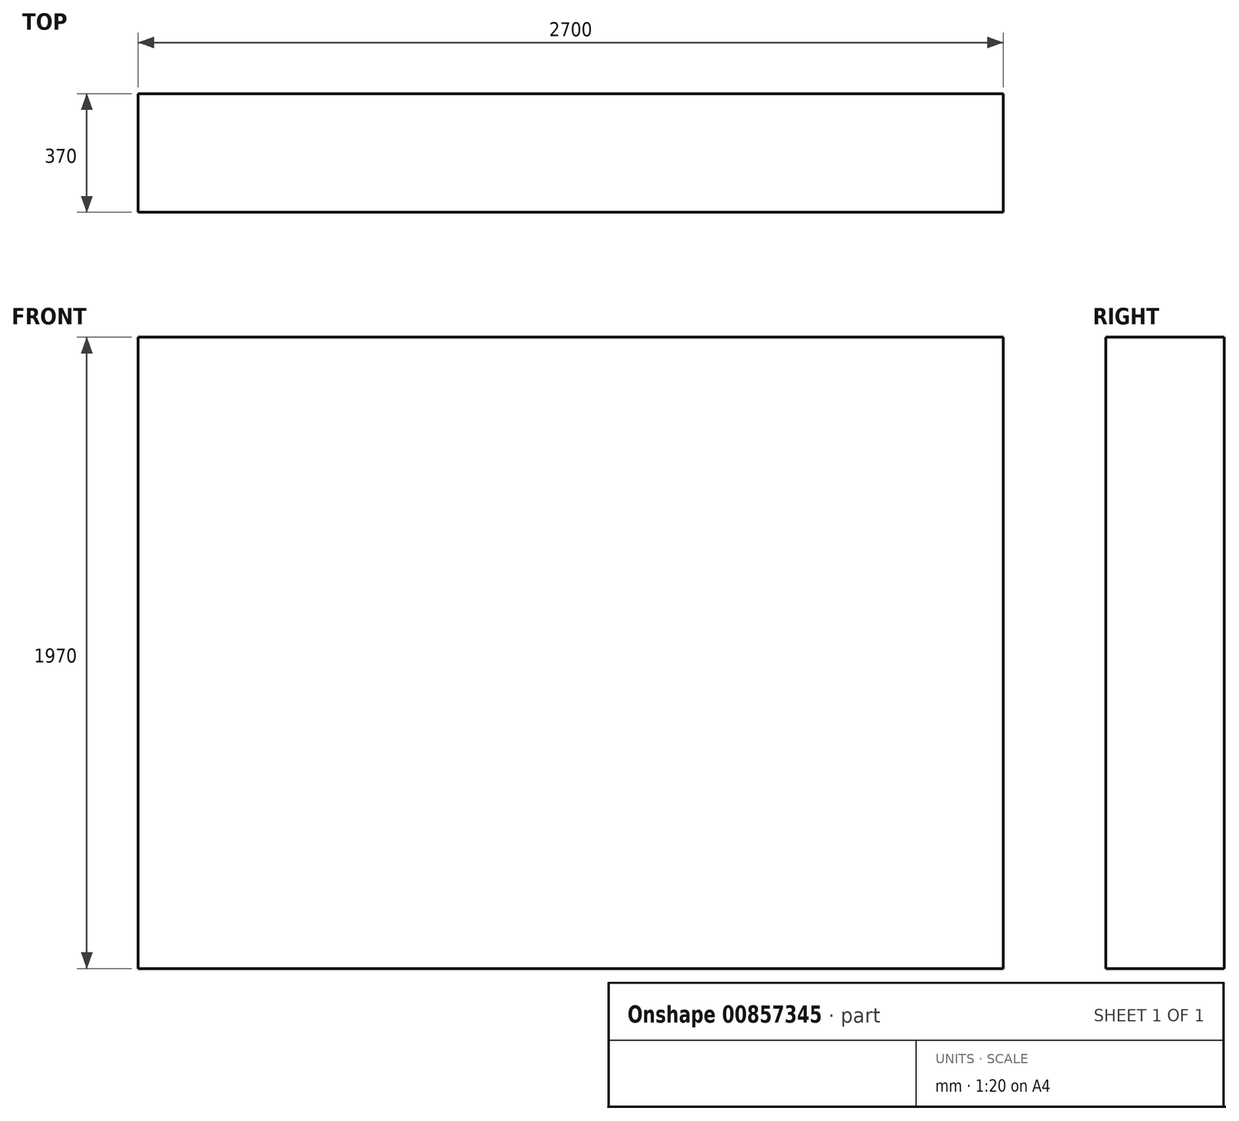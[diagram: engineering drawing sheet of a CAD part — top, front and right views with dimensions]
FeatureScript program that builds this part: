
annotation { "Feature Type Name" : "Feature", "Feature Type Description" : "" }
export const myFeature = defineFeature(function(context is Context, id is Id, definition is map)
    precondition{}
    {
        {
            var Q0;
            Q0=qCreatedBy(makeId("Front.planeOp"),FACE);
            var sketch = newSketch(context, id + "F0", { "sketchPlane" : qUnion([Q0])});
            skLineSegment(sketch, "E0.bottom", {"start": v(0, 0) * mm, "end": v(2700, 0) * mm});
            skLineSegment(sketch, "E0.top", {"start": v(0, 1970) * mm, "end": v(2700, 1970) * mm});
            skLineSegment(sketch, "E0.left", {"start": v(0, 0) * mm, "end": v(0, 1970) * mm});
            skLineSegment(sketch, "E0.right", {"start": v(2700, 0) * mm, "end": v(2700, 1970) * mm});
            skSolve(sketch);
        }
        {
            var Q0;
            Q0 = qSketchRegion(id + "F0", true);
            extrude(context, id + "F1", {"entities" : qUnion([Q0]), "depth" : 370 * mm, "offsetDistance" : 25.4 * mm});
        }
    });
